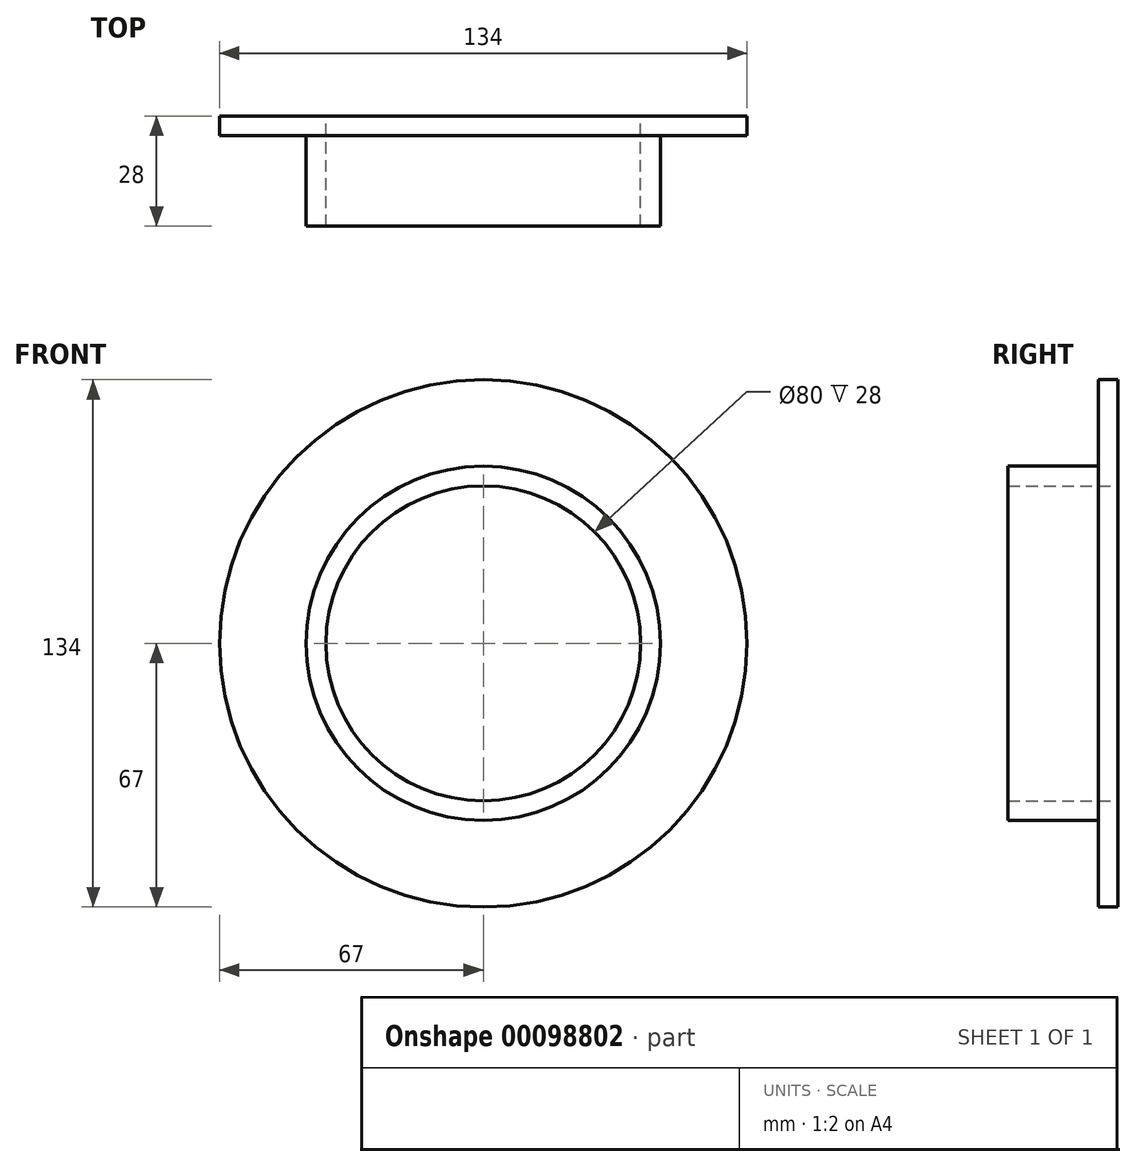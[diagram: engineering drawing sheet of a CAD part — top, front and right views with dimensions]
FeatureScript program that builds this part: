
annotation { "Feature Type Name" : "Feature", "Feature Type Description" : "" }
export const myFeature = defineFeature(function(context is Context, id is Id, definition is map)
    precondition{}
    {
        {
            var Q0;
            Q0=qCreatedBy(makeId("Top.planeOp"),FACE);
            var sketch = newSketch(context, id + "F0", { "sketchPlane" : qUnion([Q0])});
            skLineSegment(sketch, "E0", {"start": v(0, 95.6) * mm, "end": v(0, -99.99) * mm, "construction": true});
            skLineSegment(sketch, "E1", {"start": v(40, 22) * mm, "end": v(67, 22) * mm});
            skLineSegment(sketch, "E2", {"start": v(67, 17) * mm, "end": v(45, 17) * mm});
            skLineSegment(sketch, "E3", {"start": v(45, 17) * mm, "end": v(45, -6) * mm});
            skLineSegment(sketch, "E4", {"start": v(45, -6) * mm, "end": v(40, -6) * mm});
            skLineSegment(sketch, "E5", {"start": v(40, -6) * mm, "end": v(40, 22) * mm});
            skLineSegment(sketch, "E6", {"start": v(67, 22) * mm, "end": v(67, 17) * mm});
            skSolve(sketch);
        }
        {
            var Q0;
            Q0 = qSketchRegion(id + "F0", true);
            var Q1;
            Q1=sQuery(id+"F0.wireOp",EDGE,"E0");
            revolve(context, id + "F1", {"entities" : qUnion([Q0]), "axis" : qUnion([Q1]), "revolveType" : RevolveType.FULL});
        }
    });
